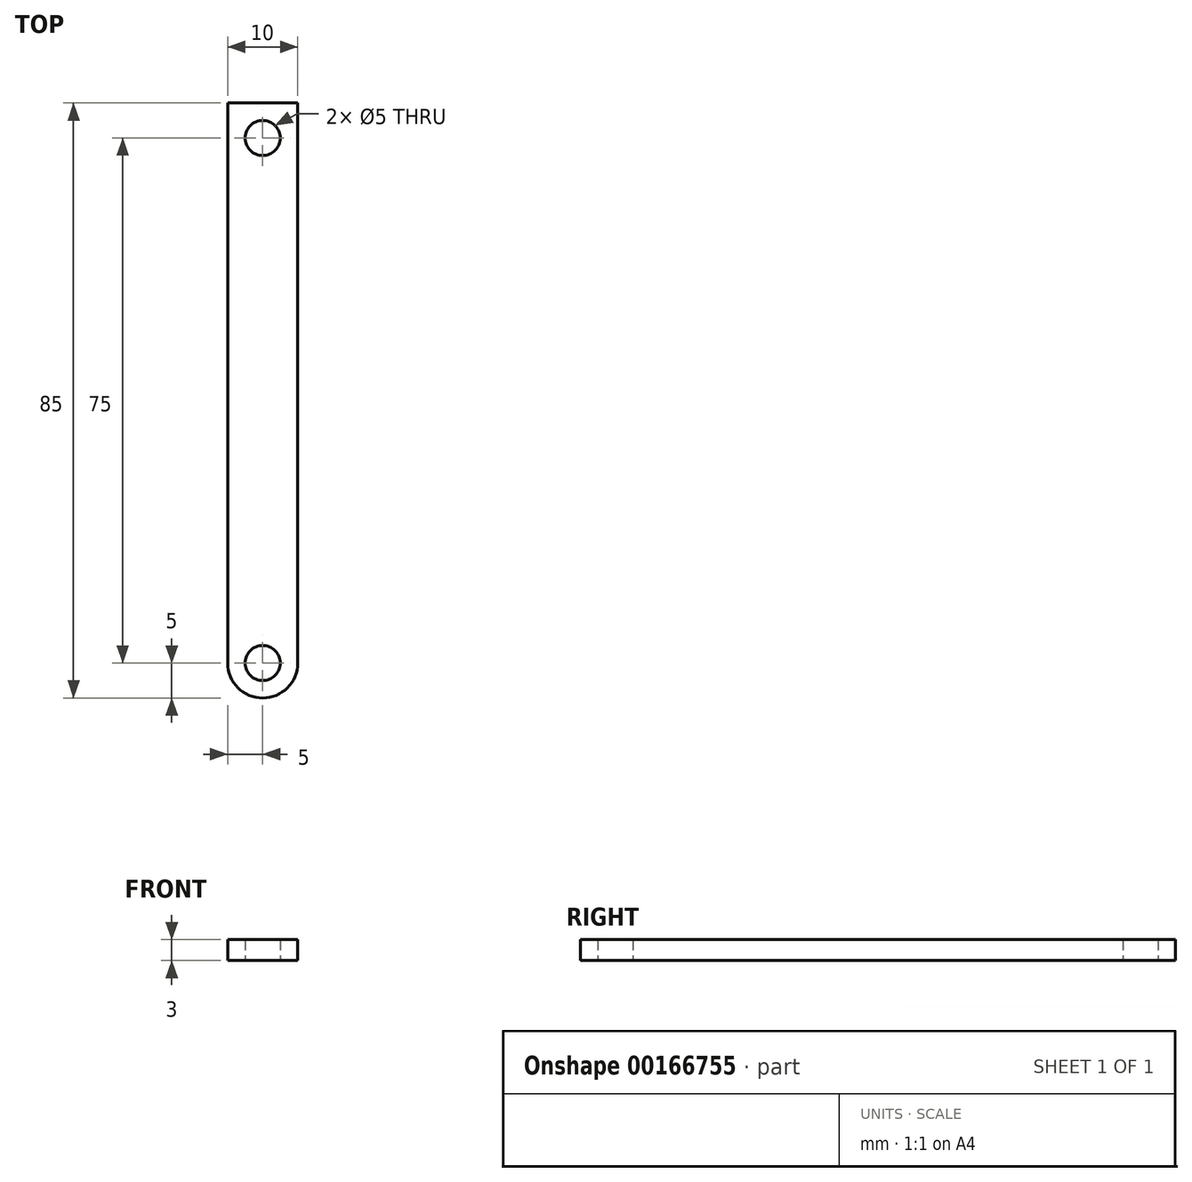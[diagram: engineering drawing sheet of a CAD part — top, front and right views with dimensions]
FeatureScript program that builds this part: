
annotation { "Feature Type Name" : "Feature", "Feature Type Description" : "" }
export const myFeature = defineFeature(function(context is Context, id is Id, definition is map)
    precondition{}
    {
        {
            var Q0;
            Q0=qCreatedBy(makeId("Top.planeOp"),FACE);
            var sketch = newSketch(context, id + "F0", { "sketchPlane" : qUnion([Q0])});
            skLineSegment(sketch, "E0.bottom", {"start": v(-5, -40) * mm, "end": v(5, -40) * mm});
            skLineSegment(sketch, "E0.top", {"start": v(-5, 40) * mm, "end": v(5, 40) * mm});
            skLineSegment(sketch, "E0.left", {"start": v(-5, -40) * mm, "end": v(-5, 40) * mm});
            skLineSegment(sketch, "E0.right", {"start": v(5, -40) * mm, "end": v(5, 40) * mm});
            skArc(sketch, "E1", {"start": v(-5, -40) * mm, "mid": v(0, -45) * mm, "end": v(5, -40) * mm});
            skCircle(sketch, "E2", {"center": v(0, 35) * mm, "radius": 2.5 * mm});
            skCircle(sketch, "E3", {"center": v(0, -40) * mm, "radius": 2.5 * mm});
            skSolve(sketch);
        }
        {
            var Q0;
            Q0=makeQuery(id+"F0.imprint","IMPRINT",FACE,{"disambiguationData":[TD([[makeQuery(id+"F0.imprint","IMPRINT",EDGE,{"derivedFrom":sQuery(id+"F0.wireOp",EDGE,"E0.top")}),-1.0]])]});
            var Q1;
            {var subQ0=sQuery(id+"F0.wireOp",EDGE,"E1");Q1=makeQuery(id+"F0.imprint","IMPRINT",FACE,{"disambiguationData":[TD([[makeQuery(id+"F0.imprint","IMPRINT",EDGE,{"derivedFrom":subQ0}),1.0]])]});}
            extrude(context, id + "F1", {"entities" : qUnion([Q0, Q1]), "depth" : 3 * mm});
        }
    });
